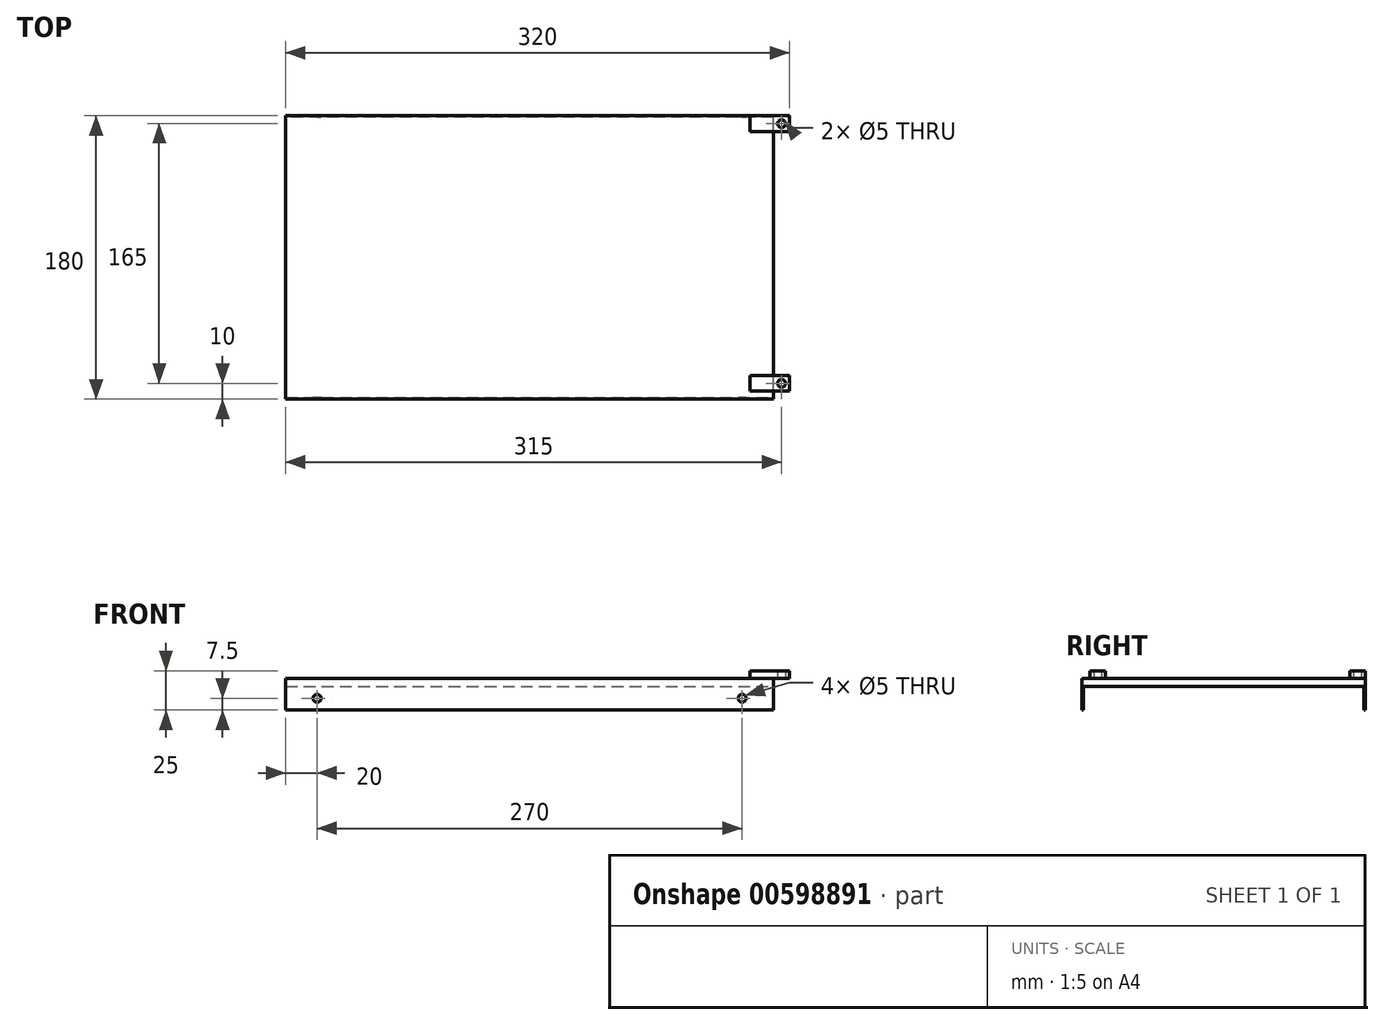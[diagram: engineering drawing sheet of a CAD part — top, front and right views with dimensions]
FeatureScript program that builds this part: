
annotation { "Feature Type Name" : "Feature", "Feature Type Description" : "" }
export const myFeature = defineFeature(function(context is Context, id is Id, definition is map)
    precondition{}
    {
        {
            var Q0;
            Q0=qCreatedBy(makeId("Top.planeOp"),FACE);
            var sketch = newSketch(context, id + "F0", { "sketchPlane" : qUnion([Q0])});
            skLineSegment(sketch, "E0.bottom", {"start": v(155, -90) * mm, "end": v(-155, -90) * mm});
            skLineSegment(sketch, "E0.top", {"start": v(155, 90) * mm, "end": v(-155, 90) * mm});
            skLineSegment(sketch, "E0.left", {"start": v(155, -90) * mm, "end": v(155, 90) * mm});
            skLineSegment(sketch, "E0.right", {"start": v(-155, -90) * mm, "end": v(-155, 90) * mm});
            skPoint(sketch, "E0.middle", {"position": v(0, 0) * mm});
            skSolve(sketch);
        }
        {
            var Q0;
            Q0=qSketchRegion(id+"F0",true);
            extrude(context, id + "F1", {"entities" : qUnion([Q0]), "depth" : 5 * mm, "offsetDistance" : 25 * mm});
        }
        {
            var Q0;
            Q0=makeQuery(id+"F1.opExtrude","CAP_FACE",FACE,{"disambiguationData":[OSD([sQuery(id+"F0.wireOp",EDGE,"E0.bottom"),sQuery(id+"F0.wireOp",EDGE,"E0.top"),sQuery(id+"F0.wireOp",EDGE,"E0.left"),sQuery(id+"F0.wireOp",EDGE,"E0.right")])],"isStart":false});
            var sketch = newSketch(context, id + "F2", { "sketchPlane" : qUnion([Q0])});
            skLineSegment(sketch, "E1.bottom", {"start": v(140, 90) * mm, "end": v(165, 90) * mm});
            skLineSegment(sketch, "E1.top", {"start": v(140, 80) * mm, "end": v(165, 80) * mm});
            skLineSegment(sketch, "E1.left", {"start": v(140, 90) * mm, "end": v(140, 80) * mm});
            skLineSegment(sketch, "E1.right", {"start": v(165, 90) * mm, "end": v(165, 80) * mm});
            skSolve(sketch);
        }
        {
            var Q0;
            Q0=qSketchRegion(id+"F2",true);
            extrude(context, id + "F3", {"entities" : qUnion([Q0]), "operationType" : NewBodyOperationType.ADD, "depth" : 5 * mm, "offsetDistance" : 25 * mm});
        }
        {
            var Q0;
            Q0=makeQuery(id+"F3.opExtrude","CAP_FACE",FACE,{"disambiguationData":[OSD([sQuery(id+"F2.wireOp",EDGE,"E1.bottom"),sQuery(id+"F2.wireOp",EDGE,"E1.top"),sQuery(id+"F2.wireOp",EDGE,"E1.left"),sQuery(id+"F2.wireOp",EDGE,"E1.right")])],"isStart":false});
            var sketch = newSketch(context, id + "F4", { "sketchPlane" : qUnion([Q0])});
            skLineSegment(sketch, "E2", {"start": v(165, 85) * mm, "end": v(160, 85) * mm});
            skSolve(sketch);
        }
        {
            var Q0;
            Q0=sQuery(id+"F4.wireOp",VERTEX,"E2.end");
            var Q1;
            Q1=makeQuery(id+"F1.opExtrude","SWEPT_BODY",BODY,{"disambiguationData":[OSD([sQuery(id+"F0.wireOp",EDGE,"E0.bottom"),sQuery(id+"F0.wireOp",EDGE,"E0.top"),sQuery(id+"F0.wireOp",EDGE,"E0.left"),sQuery(id+"F0.wireOp",EDGE,"E0.right")])]});
            hole(context, id + "F5", {"style" : HoleStyle.SIMPLE, "endStyle" : HoleEndStyle.THROUGH, "holeDiameter" : 5 * mm, "majorDiameter" : 5 * mm, "isTappedThrough" : true, "tappedDepth" : 12 * mm, "tapClearance" : 3, "locations" : qUnion([Q0]), "scope" : qUnion([Q1])});
        }
        {
            var Q0;
            Q0=makeQuery(id+"F1.opExtrude","CAP_FACE",FACE,{"disambiguationData":[OSD([sQuery(id+"F0.wireOp",EDGE,"E0.bottom"),sQuery(id+"F0.wireOp",EDGE,"E0.top"),sQuery(id+"F0.wireOp",EDGE,"E0.left"),sQuery(id+"F0.wireOp",EDGE,"E0.right")])],"isStart":false});
            var sketch = newSketch(context, id + "F6", { "sketchPlane" : qUnion([Q0])});
            skLineSegment(sketch, "E3.bottom", {"start": v(140, -85) * mm, "end": v(165, -85) * mm});
            skLineSegment(sketch, "E3.top", {"start": v(140, -75) * mm, "end": v(165, -75) * mm});
            skLineSegment(sketch, "E3.left", {"start": v(140, -85) * mm, "end": v(140, -75) * mm});
            skLineSegment(sketch, "E3.right", {"start": v(165, -85) * mm, "end": v(165, -75) * mm});
            skSolve(sketch);
        }
        {
            var Q0;
            Q0=qSketchRegion(id+"F6",true);
            extrude(context, id + "F7", {"entities" : qUnion([Q0]), "operationType" : NewBodyOperationType.ADD, "depth" : 5 * mm, "offsetDistance" : 25 * mm});
        }
        {
            var Q0;
            Q0=makeQuery(id+"F7.opExtrude","CAP_FACE",FACE,{"disambiguationData":[OSD([sQuery(id+"F6.wireOp",EDGE,"E3.bottom"),sQuery(id+"F6.wireOp",EDGE,"E3.top"),sQuery(id+"F6.wireOp",EDGE,"E3.left"),sQuery(id+"F6.wireOp",EDGE,"E3.right")])],"isStart":false});
            var sketch = newSketch(context, id + "F8", { "sketchPlane" : qUnion([Q0])});
            skLineSegment(sketch, "E4", {"start": v(165, -80) * mm, "end": v(160, -80) * mm});
            skSolve(sketch);
        }
        {
            var Q0;
            Q0=sQuery(id+"F8.wireOp",VERTEX,"E4.end");
            var Q1;
            Q1=makeQuery(id+"F1.opExtrude","SWEPT_BODY",BODY,{"disambiguationData":[OSD([sQuery(id+"F0.wireOp",EDGE,"E0.bottom"),sQuery(id+"F0.wireOp",EDGE,"E0.top"),sQuery(id+"F0.wireOp",EDGE,"E0.left"),sQuery(id+"F0.wireOp",EDGE,"E0.right")])]});
            hole(context, id + "F9", {"style" : HoleStyle.SIMPLE, "endStyle" : HoleEndStyle.THROUGH, "holeDiameter" : 5 * mm, "majorDiameter" : 5 * mm, "isTappedThrough" : true, "tappedDepth" : 12 * mm, "tapClearance" : 3, "locations" : qUnion([Q0]), "scope" : qUnion([Q1])});
        }
        {
            var Q0;
            Q0=makeQuery(id+"F1.opExtrude","CAP_FACE",FACE,{"disambiguationData":[OSD([sQuery(id+"F0.wireOp",EDGE,"E0.bottom"),sQuery(id+"F0.wireOp",EDGE,"E0.top"),sQuery(id+"F0.wireOp",EDGE,"E0.left"),sQuery(id+"F0.wireOp",EDGE,"E0.right")])],"isStart":true});
            var sketch = newSketch(context, id + "F10", { "sketchPlane" : qUnion([Q0])});
            skLineSegment(sketch, "E5.bottom", {"start": v(155, -90) * mm, "end": v(-155, -90) * mm});
            skLineSegment(sketch, "E5.top", {"start": v(155, -89) * mm, "end": v(-155, -89) * mm});
            skLineSegment(sketch, "E5.left", {"start": v(155, -90) * mm, "end": v(155, -89) * mm});
            skLineSegment(sketch, "E5.right", {"start": v(-155, -90) * mm, "end": v(-155, -89) * mm});
            skLineSegment(sketch, "E6.bottom", {"start": v(-155, 90) * mm, "end": v(155, 90) * mm});
            skLineSegment(sketch, "E6.top", {"start": v(-155, 89) * mm, "end": v(155, 89) * mm});
            skLineSegment(sketch, "E6.left", {"start": v(-155, 90) * mm, "end": v(-155, 89) * mm});
            skLineSegment(sketch, "E6.right", {"start": v(155, 90) * mm, "end": v(155, 89) * mm});
            skSolve(sketch);
        }
        {
            var Q0;
            Q0=makeQuery(id+"F10.imprint","IMPRINT",FACE,{"disambiguationData":[TD([[makeQuery(id+"F10.imprint","IMPRINT",EDGE,{"derivedFrom":sQuery(id+"F10.wireOp",EDGE,"E5.bottom")}),-1.0]])]});
            var Q1;
            Q1=makeQuery(id+"F10.imprint","IMPRINT",FACE,{"disambiguationData":[TD([[makeQuery(id+"F10.imprint","IMPRINT",EDGE,{"derivedFrom":sQuery(id+"F10.wireOp",EDGE,"E6.bottom")}),1.0]])]});
            extrude(context, id + "F11", {"entities" : qUnion([Q0, Q1]), "operationType" : NewBodyOperationType.ADD, "depth" : 15 * mm, "offsetDistance" : 25 * mm});
        }
        {
            var Q0;
            Q0=makeQuery(id+"F11.boolean.opBoolean","MERGE",FACE,{"derivedFrom":[makeQuery(id+"F3.boolean.opBoolean","MERGE",FACE,{"derivedFrom":[makeQuery(id+"F1.opExtrude","SWEPT_FACE",FACE,{"disambiguationData":[OSD([sQuery(id+"F0.wireOp",EDGE,"E0.top")])]}),makeQuery(id+"F3.opExtrude","SWEPT_FACE",FACE,{"disambiguationData":[OSD([sQuery(id+"F2.wireOp",EDGE,"E1.bottom")])]})]}),makeQuery(id+"F11.opExtrude","SWEPT_FACE",FACE,{"disambiguationData":[OSD([sQuery(id+"F10.wireOp",EDGE,"E5.bottom")])]})]});
            var sketch = newSketch(context, id + "F12", { "sketchPlane" : qUnion([Q0])});
            skLineSegment(sketch, "E7", {"start": v(-135, -15) * mm, "end": v(-135, -7.5) * mm});
            skSolve(sketch);
        }
        {
            var Q0;
            Q0=sQuery(id+"F12.wireOp",VERTEX,"E7.end");
            var Q1;
            Q1=makeQuery(id+"F1.opExtrude","SWEPT_BODY",BODY,{"disambiguationData":[OSD([sQuery(id+"F0.wireOp",EDGE,"E0.bottom"),sQuery(id+"F0.wireOp",EDGE,"E0.top"),sQuery(id+"F0.wireOp",EDGE,"E0.left"),sQuery(id+"F0.wireOp",EDGE,"E0.right")])]});
            hole(context, id + "F13", {"style" : HoleStyle.SIMPLE, "endStyle" : HoleEndStyle.THROUGH, "holeDiameter" : 5 * mm, "majorDiameter" : 5 * mm, "isTappedThrough" : true, "tappedDepth" : 12 * mm, "tapClearance" : 3, "locations" : qUnion([Q0]), "scope" : qUnion([Q1])});
        }
        {
            var Q0;
            Q0=makeQuery(id+"F11.boolean.opBoolean","MERGE",FACE,{"derivedFrom":[makeQuery(id+"F3.boolean.opBoolean","MERGE",FACE,{"derivedFrom":[makeQuery(id+"F1.opExtrude","SWEPT_FACE",FACE,{"disambiguationData":[OSD([sQuery(id+"F0.wireOp",EDGE,"E0.top")])]}),makeQuery(id+"F3.opExtrude","SWEPT_FACE",FACE,{"disambiguationData":[OSD([sQuery(id+"F2.wireOp",EDGE,"E1.bottom")])]})]}),makeQuery(id+"F11.opExtrude","SWEPT_FACE",FACE,{"disambiguationData":[OSD([sQuery(id+"F10.wireOp",EDGE,"E5.bottom")])]})]});
            var sketch = newSketch(context, id + "F14", { "sketchPlane" : qUnion([Q0])});
            skLineSegment(sketch, "E8", {"start": v(135, -15) * mm, "end": v(135, -7.5) * mm});
            skSolve(sketch);
        }
        {
            var Q0;
            Q0=sQuery(id+"F14.wireOp",VERTEX,"E8.end");
            var Q1;
            Q1=makeQuery(id+"F1.opExtrude","SWEPT_BODY",BODY,{"disambiguationData":[OSD([sQuery(id+"F0.wireOp",EDGE,"E0.bottom"),sQuery(id+"F0.wireOp",EDGE,"E0.top"),sQuery(id+"F0.wireOp",EDGE,"E0.left"),sQuery(id+"F0.wireOp",EDGE,"E0.right")])]});
            hole(context, id + "F15", {"style" : HoleStyle.SIMPLE, "endStyle" : HoleEndStyle.THROUGH, "holeDiameter" : 5 * mm, "majorDiameter" : 5 * mm, "isTappedThrough" : true, "tappedDepth" : 12 * mm, "tapClearance" : 3, "locations" : qUnion([Q0]), "scope" : qUnion([Q1])});
        }
    });
